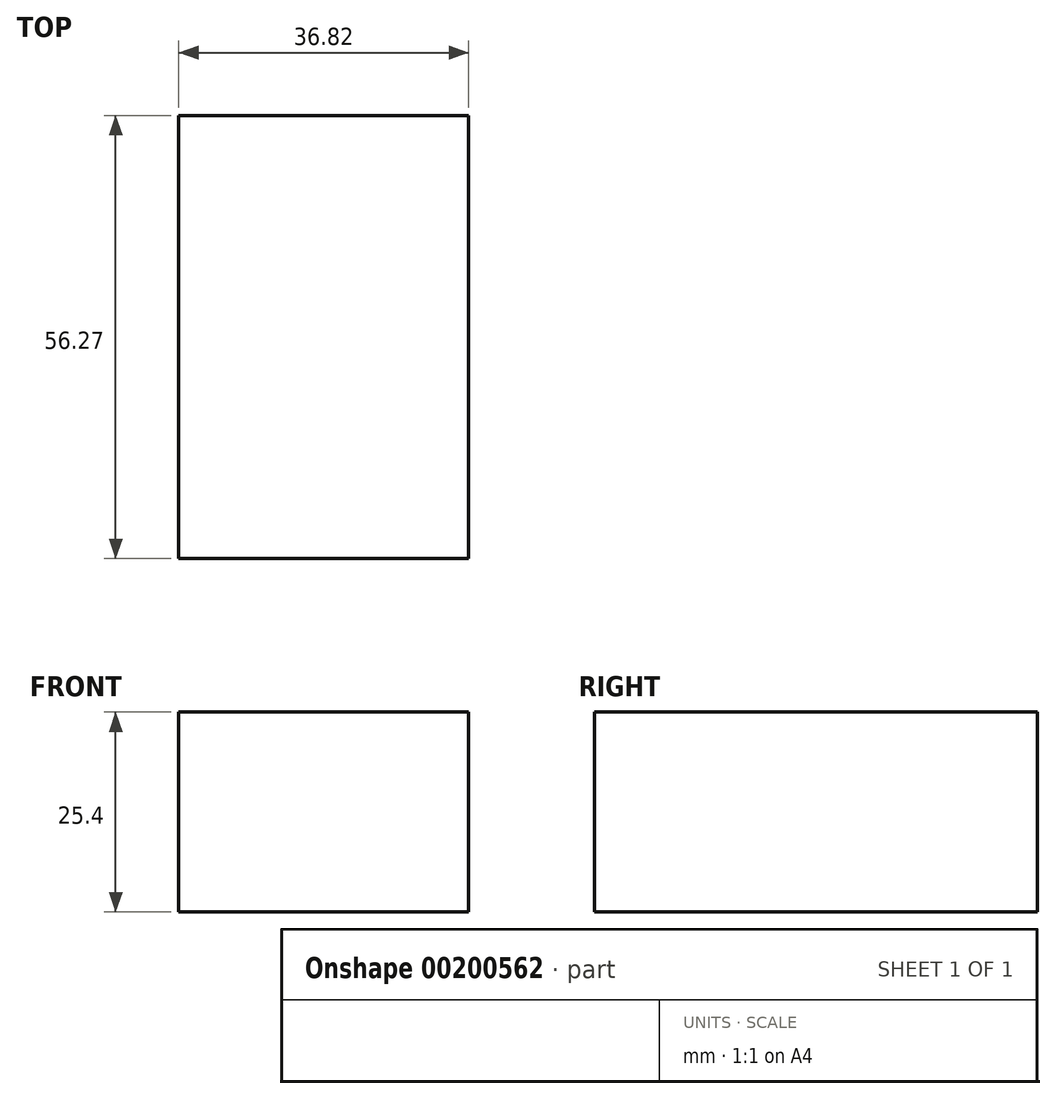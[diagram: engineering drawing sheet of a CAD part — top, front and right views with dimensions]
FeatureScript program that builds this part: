
annotation { "Feature Type Name" : "Feature", "Feature Type Description" : "" }
export const myFeature = defineFeature(function(context is Context, id is Id, definition is map)
    precondition{}
    {
        {
            var Q0;
            Q0=qCreatedBy(makeId("Top.planeOp"),FACE);
            var sketch = newSketch(context, id + "F0", { "sketchPlane" : qUnion([Q0])});
            skLineSegment(sketch, "E0.bottom", {"start": v(-28.83, 25.78) * mm, "end": v(44.8, 25.78) * mm});
            skLineSegment(sketch, "E0.top", {"start": v(-28.83, -30.5) * mm, "end": v(44.8, -30.5) * mm});
            skLineSegment(sketch, "E0.left", {"start": v(-28.83, 25.78) * mm, "end": v(-28.83, -30.5) * mm});
            skLineSegment(sketch, "E0.right", {"start": v(44.8, 25.78) * mm, "end": v(44.8, -30.5) * mm});
            skLineSegment(sketch, "E1", {"start": v(7.99, 25.78) * mm, "end": v(7.99, -30.5) * mm});
            skSolve(sketch);
        }
        {
            var Q0;
            {var subQ0=sQuery(id+"F0.wireOp",EDGE,"E0.left");Q0=makeQuery(id+"F0.imprint","IMPRINT",FACE,{"disambiguationData":[TD([[makeQuery(id+"F0.imprint","IMPRINT",EDGE,{"derivedFrom":subQ0}),1.0]])]});}
            extrude(context, id + "F1", {"entities" : qUnion([Q0]), "depth" : 25.4 * mm});
        }
    });
